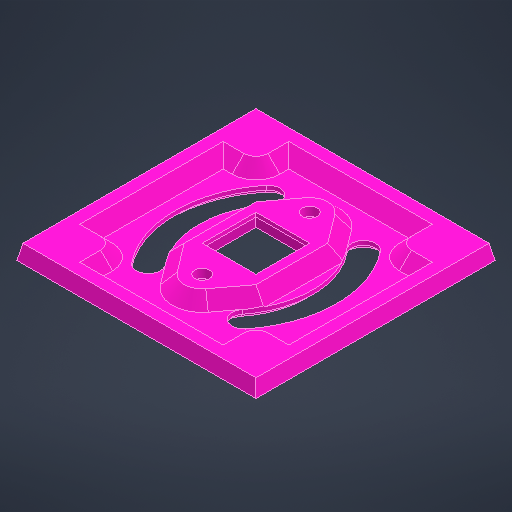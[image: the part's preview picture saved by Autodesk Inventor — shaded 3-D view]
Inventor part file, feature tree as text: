
AUTODESK INVENTOR PART (.ipt)
format: ipt  version: 2025.1 (Build 291241000, 241)  size: 722,944 bytes
history: native  units: mm
features: chamfer x5, extrude x4, sketch x2, projected_geometry x1
ambient origin geometry x8: Origin, YZ Plane, XZ Plane, XY Plane, X Axis, Y Axis, Z Axis, Center Point
bodies: Solid1 (feature_tree)
feature tree (12):
  sketch  "Sketch1"  dims[d0=40.0mm d2=9.0mm]
  extrude  "Extrusion1"  Depth=9.0mm
  extrude  "Extrusion3"  Depth=2.5mm
  extrude  "Extrusion2"  Depth=4.0mm
  chamfer  "Chamfer7"  Distance=28.0mm
  chamfer  "Chamfer8"  Distance=1.7mm
  chamfer  "Chamfer9"  Distance=2.2mm
  chamfer  "Chamfer11"  Distance=2.0mm
  extrude  "Extrusion5"  Depth=1.5mm
  chamfer  "Chamfer10"  Distance=6.0mm
  sketch  "Sketch2"  dims[d3=2.5mm d4=9.0mm d5=4.0mm d6=2.5mm d7=9.0mm d8=4.0mm d12=2.5mm d14=4.0mm d16=4.0mm d17=28.0mm d18=1.7mm d19=0.0mm d20=2.2mm d21=0.0mm d22=2.0mm d23=0.0mm d27=2.6mm d45=6.0mm d48=1.5mm d49=2.5mm d50=2.0mm d51=2.0mm d52=45.0deg d53=0.5mm d54=2.5mm d55=45.0deg d56=3.0mm d57=1.2mm d58=45.0deg d59=20.0mm d60=8.0mm d62=0.0mm d63=0.0mm d64=1.0mm d65=2.0mm d66=45.0deg d67=1.5mm d68=3.0mm d69=45.0deg d70=4.0mm d71=1.5mm]
  projected_geometry  "Projected Loop1"
